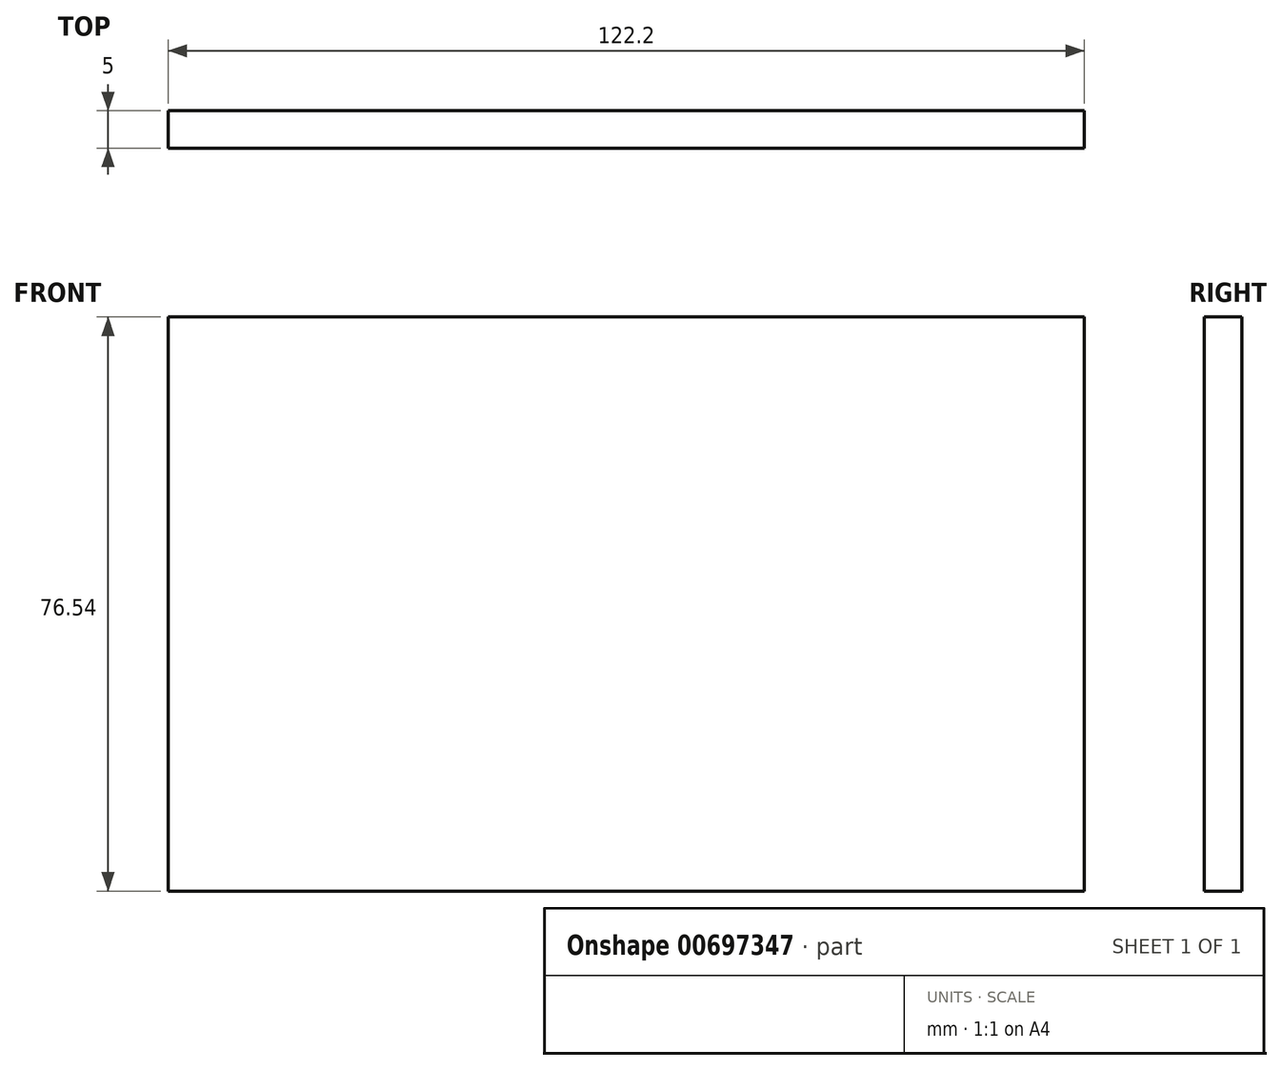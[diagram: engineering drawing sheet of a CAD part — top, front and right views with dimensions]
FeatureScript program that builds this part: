
annotation { "Feature Type Name" : "Feature", "Feature Type Description" : "" }
export const myFeature = defineFeature(function(context is Context, id is Id, definition is map)
    precondition{}
    {
        {
            var Q0;
            Q0=qCreatedBy(makeId("Front.planeOp"),FACE);
            var sketch = newSketch(context, id + "F0", { "sketchPlane" : qUnion([Q0])});
            skLineSegment(sketch, "E0.bottom", {"start": v(0, 0) * mm, "end": v(-122.2, 0) * mm});
            skLineSegment(sketch, "E0.top", {"start": v(0, 76.54) * mm, "end": v(-122.2, 76.54) * mm});
            skLineSegment(sketch, "E0.left", {"start": v(0, 0) * mm, "end": v(0, 76.54) * mm});
            skLineSegment(sketch, "E0.right", {"start": v(-122.2, 0) * mm, "end": v(-122.2, 76.54) * mm});
            skSolve(sketch);
        }
        {
            var Q0;
            Q0 = qSketchRegion(id + "F0", true);
            extrude(context, id + "F1", {"entities" : qUnion([Q0]), "depth" : 5 * mm, "offsetDistance" : 25 * mm});
        }
    });
